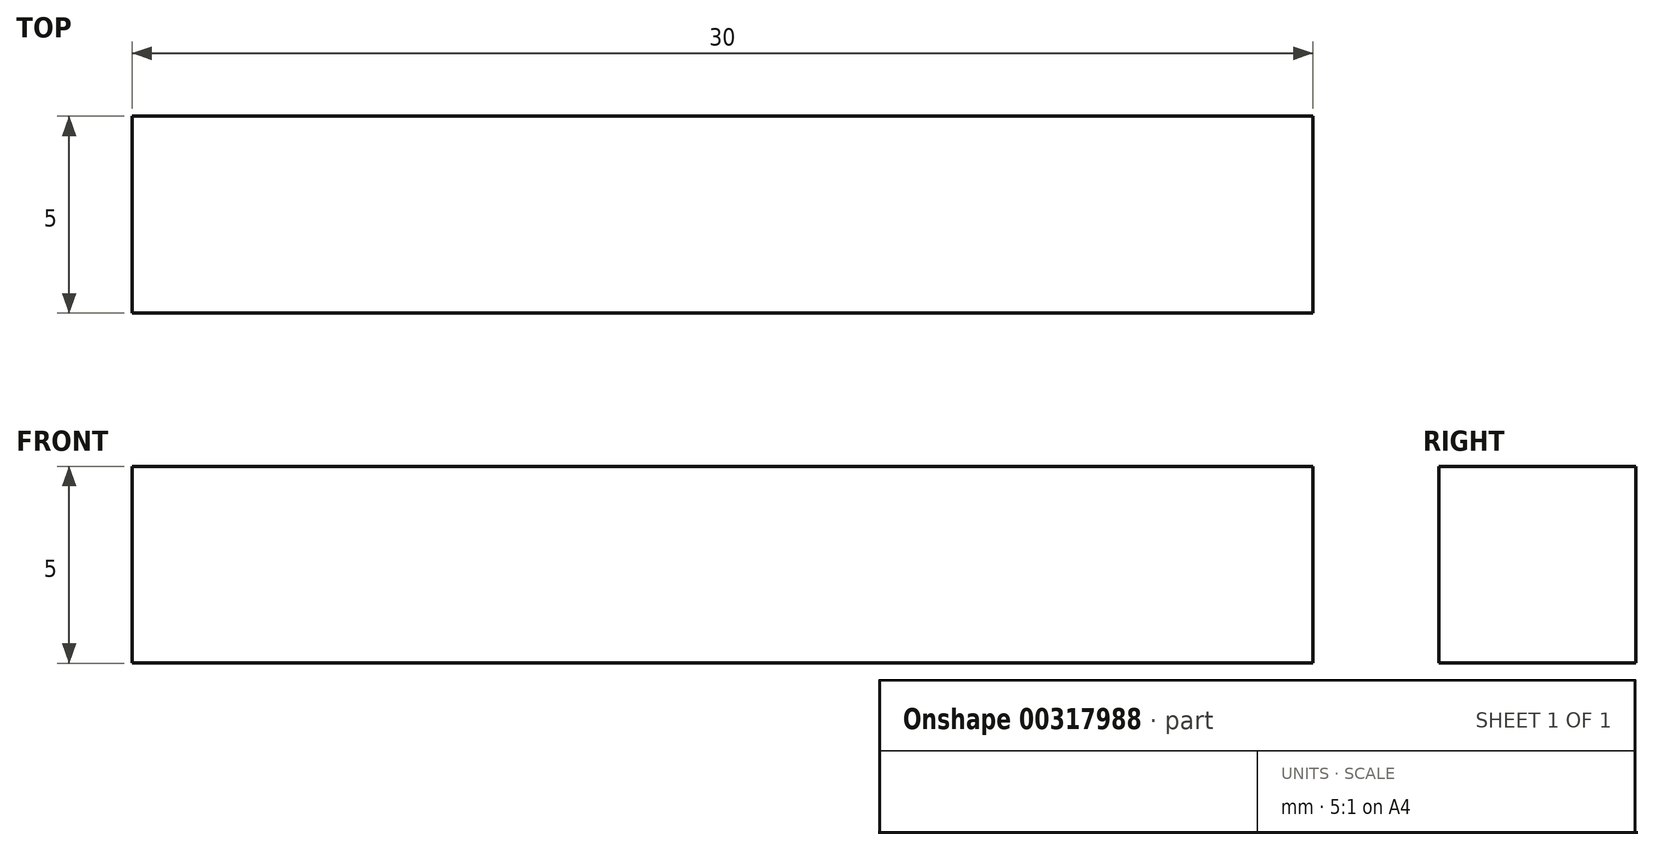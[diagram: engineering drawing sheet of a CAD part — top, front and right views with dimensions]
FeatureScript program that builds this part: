
annotation { "Feature Type Name" : "Feature", "Feature Type Description" : "" }
export const myFeature = defineFeature(function(context is Context, id is Id, definition is map)
    precondition{}
    {
        {
            var Q0;
            Q0=qCreatedBy(makeId("Front.planeOp"),FACE);
            var sketch = newSketch(context, id + "F0", { "sketchPlane" : qUnion([Q0])});
            skLineSegment(sketch, "E0.bottom", {"start": v(-16.35, 2.38) * mm, "end": v(13.65, 2.38) * mm});
            skLineSegment(sketch, "E0.top", {"start": v(-16.35, -2.62) * mm, "end": v(13.65, -2.62) * mm});
            skLineSegment(sketch, "E0.left", {"start": v(-16.35, 2.38) * mm, "end": v(-16.35, -2.62) * mm});
            skLineSegment(sketch, "E0.right", {"start": v(13.65, 2.38) * mm, "end": v(13.65, -2.62) * mm});
            skSolve(sketch);
        }
        {
            var Q0;
            Q0=makeQuery(id+"F0.imprint","IMPRINT",FACE,{"disambiguationData":[TD([[makeQuery(id+"F0.imprint","IMPRINT",EDGE,{"derivedFrom":sQuery(id+"F0.wireOp",EDGE,"E0.bottom")}),-1.0]])]});
            extrude(context, id + "F1", {"entities" : qUnion([Q0]), "depth" : 5 * mm});
        }
    });
